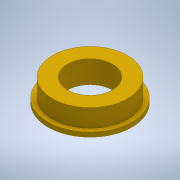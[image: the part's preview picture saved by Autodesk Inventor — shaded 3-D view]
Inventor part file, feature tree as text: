
AUTODESK INVENTOR PART (.ipt)
format: ipt  version: 2020.2 (Build 242310000, 310)  size: 128,000 bytes
history: native  units: mm
features: extrude x2, other x1, sketch x1
ambient origin geometry x8: Origin, YZ Plane, XZ Plane, XY Plane, X Axis, Y Axis, Z Axis, Center Point
bodies: Body1 (feature_tree)
feature tree (4):
  other  "ソリッド1"
  sketch  "スケッチ1"
  extrude  "押し出し1"  Depth=10.0mm
  extrude  "押し出し2"  Depth=6.0mm
